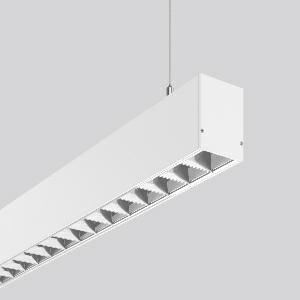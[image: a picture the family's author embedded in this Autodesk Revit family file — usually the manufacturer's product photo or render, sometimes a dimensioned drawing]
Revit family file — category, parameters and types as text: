
# Revit family: less_is_more_50_312345_002_1_31c8
name_source: partatom
category: Lighting Fixtures
units: mm (PartAtom-declared; Revit-internal decimal feet)

## family parameters
Cut with Voids When Loaded = No
Host = Face
Light Source = No
Part Type = Normal
Room Calculation Point = No
Round Connector Dimension = Use Diameter
Shared = No

## types (1)
- LESS IS MORE 50 (1 x LED Modul 840, 9250 lm, 4000)
    Apparent Load = 76 VA
    CIE Flux Codes = 95 100 100 63 100
    Color Rendering = 80
    Color Temperature = 4000
    Default Elevation = 1800 mm
    Description = Series: LESS IS MORE 50
Linear pendant luminaire for aesthetically sophisticated lighting. Housing: extruded aluminium profile, powder-coated. End cap aluminium powder-coated. Canopy made of aluminium, powder-coated. Alea optical system: Reflector structure (ABS, Aluminium-coated, highly polished) with integrated diffuser made of non-yellowing plastic (PMMA) opal for glare-free light at the workstation (screen-compliant according to EN 12464-1). Direct 65%, indirect 35% light emission. Suitable for pendant. 2-point steel cable suspension freely positionable and infinitely height-adjustable. Special lengths available on request. LED unit with integrated converter interchangeable and removable. Suitable for through-wiring. With sensors or as a safety luminaire on request. 
Colour: traffic white, matt (RAL 9016)
Length: 1967 mm
Width: 57 mm
Height: 75 mm
Suspension length: 2000 mm
Lamp: LED
Socket: without socket
Colour temperature: 4000K
Colour rendering index (CRI): 80
Light source: LED
Socket lamp2: Without base
Colour temperature: 4000K
System power: 76 W
Rated luminous flux: 9250 lm
Luminous efficiency: 122 lm/W
Control gear: Regulated power supply
Control gear: Regulated power supply
Protection class: I
Type of protection: IP 20
    Height = 75 mm
    Lamp = 1 x LED Modul 840
    Lamp Light Flux = 9250 lm
    Lamp count = 1
    Length = 1967 mm
    Lifetime = 50000 h
    Luminous efficacy = 122 lm/W
    Manufacturer = RZB
    ModVariant = No
    Model = 312345.002.1
    Mounting Place = Ceiling
    Mounting Type = Pendant
    Number of Poles = 1
    OnlyDefault = Yes
    Power Factor = 1
    Product Name = LESS IS MORE 50
    Product group = Pendant LED linear luminaires
    ProductGroupID = 907
    Protection Class = Protection class I
    Protection Degree = IP 20
    RLX_Detail_Level = 1
    RLX_Emergency_Light_Flux = 0 lm
    RLX_Emergency_Type = 0
    RLX_Emergency_Type_DB = No
    RlxData = <blob elided: 37385 chars, md5=8dac7d1d>
    Socket = socket
    Standby Power = 0 W
    System Light Flux = 9250 lm
    System Power = 76 W
    Type Comments = Product without accessories
    Type Image = 312342.002.jpg
    URL = http://relux.com
    VarID = ---
    Voltage = 230 V
    Voltage Range = 220-240 V
    Weight = 0.00 kg
    Width = 57 mm

## geometry (parser evidence)
native form markers: Blend x4, Sweep x12
no freeform markers — native parametric forms only
